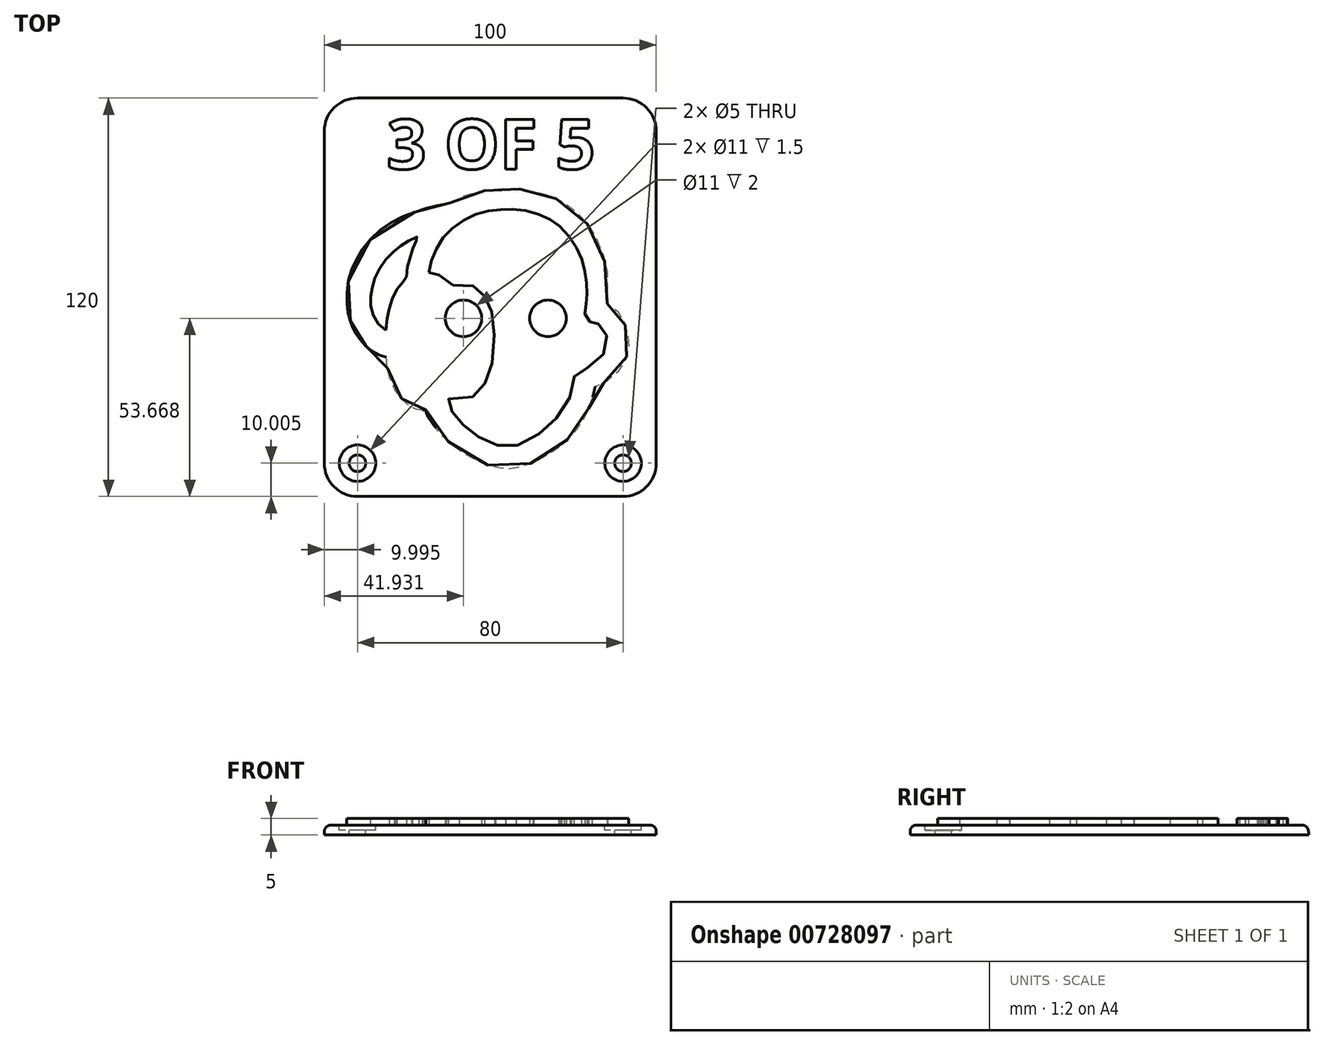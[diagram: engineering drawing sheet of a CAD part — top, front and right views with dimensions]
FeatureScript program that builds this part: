
annotation { "Feature Type Name" : "Feature", "Feature Type Description" : "" }
export const myFeature = defineFeature(function(context is Context, id is Id, definition is map)
    precondition{}
    {
        {
            var Q0;
            Q0=qCreatedBy(makeId("Top.planeOp"),FACE);
            var sketch = newSketch(context, id + "F0", { "sketchPlane" : qUnion([Q0])});
            skLineSegment(sketch, "E0.bottom", {"start": v(-46.51, 69.3) * mm, "end": v(33.49, 69.3) * mm});
            skLineSegment(sketch, "E0.top", {"start": v(-46.51, -50.7) * mm, "end": v(33.49, -50.7) * mm});
            skLineSegment(sketch, "E0.left", {"start": v(-56.51, 59.3) * mm, "end": v(-56.51, -40.7) * mm});
            skLineSegment(sketch, "E0.right", {"start": v(43.49, 59.3) * mm, "end": v(43.49, -40.7) * mm});
            skPoint(sketch, "E1.visualSharp", {"position": v(-56.51, 69.3) * mm});
            skArc(sketch, "E1.filletArc", {"start": v(-46.51, 69.3) * mm, "mid": v(-53.59, 66.38) * mm, "end": v(-56.51, 59.3) * mm});
            skPoint(sketch, "E2.visualSharp", {"position": v(43.49, 69.3) * mm});
            skArc(sketch, "E2.filletArc", {"start": v(43.49, 59.3) * mm, "mid": v(40.56, 66.38) * mm, "end": v(33.49, 69.3) * mm});
            skPoint(sketch, "E3.visualSharp", {"position": v(-56.51, -50.7) * mm});
            skArc(sketch, "E3.filletArc", {"start": v(-56.51, -40.7) * mm, "mid": v(-53.59, -47.77) * mm, "end": v(-46.51, -50.7) * mm});
            skPoint(sketch, "E4.visualSharp", {"position": v(43.49, -50.7) * mm});
            skArc(sketch, "E4.filletArc", {"start": v(33.49, -50.7) * mm, "mid": v(40.56, -47.77) * mm, "end": v(43.49, -40.7) * mm});
            skSolve(sketch);
        }
        {
            var Q0;
            Q0 = qSketchRegion(id + "F0", true);
            extrude(context, id + "F1", {"entities" : qUnion([Q0]), "depth" : 3 * mm, "offsetDistance" : 25 * mm});
        }
        {
            var Q0;
            Q0=makeQuery(id+"F1.opExtrude","CAP_FACE",FACE,{"disambiguationData":[OSD([sQuery(id+"F0.wireOp",EDGE,"E0.bottom"),sQuery(id+"F0.wireOp",EDGE,"E0.top"),sQuery(id+"F0.wireOp",EDGE,"E0.left"),sQuery(id+"F0.wireOp",EDGE,"E0.right")])],"isStart":false});
            var sketch = newSketch(context, id + "F2", { "sketchPlane" : qUnion([Q0])});
            skFitSpline(sketch, "E5", {"points": [v(-25.07, 16.79) * mm, v(-23.95, 21.02) * mm, v(-21.7, 25.75) * mm, v(-18.34, 29.73) * mm, v(-13.49, 33.1) * mm, v(-8.76, 34.96) * mm, v(-3.78, 35.7) * mm, v(0, 35.83) * mm, v(5.54, 35.09) * mm, v(10.56, 33.2) * mm, v(14.02, 30.98) * mm, v(17.76, 26.87) * mm, v(20.5, 22.26) * mm, v(21.92, 17.56) * mm, v(22.5, 13.37) * mm, v(22.6, 9.8) * mm, v(22.28, 6.72) * mm, v(22.08, 3.84) * mm, v(23.6, 1.85) * mm, v(26.1, 1.25) * mm], "startDerivative": vector(17.63, 78.8) * mm, "endDerivative": vector(72.1, -32.78) * mm});
            skFitSpline(sketch, "E6", {"points": [v(26.1, 1.25) * mm, v(26.68, 0.97) * mm, v(27.3, 0.48) * mm, v(27.8, -0.36) * mm, v(28.13, -1.04) * mm, v(28.4, -1.76) * mm, v(28.71, -2.9) * mm, v(28.77, -4.2) * mm, v(28.58, -5.64) * mm, v(28.2, -6.83) * mm, v(27.44, -8) * mm, v(26.4, -9.15) * mm, v(24.92, -10.44) * mm, v(23.87, -11.27) * mm, v(22.55, -12) * mm, v(21.27, -12.13) * mm, v(20.46, -12.4) * mm, v(19.66, -12.89) * mm, v(19.16, -13.65) * mm, v(18.78, -14.9) * mm, v(18.63, -16.3) * mm, v(18.59, -17.55) * mm, v(18, -19.6) * mm, v(17.12, -21.66) * mm, v(16.06, -23.69) * mm, v(14.7, -25.67) * mm, v(13.38, -27.2) * mm, v(12.1, -28.57) * mm, v(10.52, -30.02) * mm, v(9.07, -31.12) * mm, v(7.35, -32.36) * mm, v(5.5, -33.41) * mm, v(2.92, -34.68) * mm, v(1.71, -35.23) * mm, v(0.27, -35.65) * mm, v(-0.64, -35.78) * mm, v(-2.05, -35.8) * mm, v(-3.83, -35.5) * mm, v(-5.21, -35.07) * mm, v(-6.81, -34.41) * mm, v(-8.49, -33.55) * mm, v(-9.64, -32.95) * mm, v(-10.87, -32.21) * mm, v(-12, -31.43) * mm, v(-12.96, -30.64) * mm, v(-13.98, -29.7) * mm, v(-14.79, -28.98) * mm, v(-15.62, -28.12) * mm, v(-16.35, -27.27) * mm, v(-17.16, -26.3) * mm, v(-17.82, -25.44) * mm, v(-18.46, -24.6) * mm, v(-18.99, -23.77) * mm, v(-19.5, -22.87) * mm, v(-19.8, -22.23) * mm, v(-19.76, -21.68) * mm, v(-18.92, -21.3) * mm, v(-18.3, -21.07) * mm, v(-17.58, -20.66) * mm, v(-16.72, -20.66) * mm, v(-11.7, -20.62) * mm, v(-10.67, -20.14) * mm, v(-10.07, -19.5) * mm, v(-9.23, -18.44) * mm, v(-8.55, -17.35) * mm, v(-7.7, -15.82) * mm, v(-7.05, -14.33) * mm, v(-6.59, -12.83) * mm, v(-6.15, -11.25) * mm, v(-5.76, -8.98) * mm, v(-5.51, -5.8) * mm, v(-5.33, -3) * mm, v(-5.26, 0) * mm, v(-5.35, 1.51) * mm, v(-5.66, 3.34) * mm, v(-6.08, 5.06) * mm, v(-6.48, 6.3) * mm, v(-7, 7.46) * mm, v(-7.48, 8.45) * mm, v(-7.84, 9.08) * mm, v(-8.32, 9.84) * mm, v(-8.76, 10.44) * mm, v(-9.2, 11) * mm, v(-9.86, 11.62) * mm, v(-10.78, 12.25) * mm, v(-11.49, 12.66) * mm, v(-12.24, 12.87) * mm, v(-14.3, 12.85) * mm, v(-15.8, 12.81) * mm, v(-17.19, 12.86) * mm, v(-18.31, 13.27) * mm, v(-19.4, 13.91) * mm, v(-20.33, 14.64) * mm, v(-21.03, 15.21) * mm, v(-21.74, 15.8) * mm, v(-22.29, 16.27) * mm, v(-22.8, 16.68) * mm, v(-23.06, 16.73) * mm, v(-23.62, 16.73) * mm, v(-24.15, 16.72) * mm, v(-24.51, 16.71) * mm, v(-24.87, 16.7) * mm, v(-25.07, 16.79) * mm], "startDerivative": vector(82.47, -38.35) * mm, "endDerivative": vector(-44.86, 24.31) * mm});
            skCircle(sketch, "E7", {"center": v(10.87, 2.97) * mm, "radius": 5.5 * mm});
            skCircle(sketch, "E8", {"center": v(-14.58, 2.97) * mm, "radius": 5.5 * mm});
            skFitSpline(sketch, "E9", {"points": [v(-38, -0.58) * mm, v(-37.64, 1.98) * mm, v(-37.38, 3.87) * mm, v(-37, 5.76) * mm, v(-36.45, 7.58) * mm, v(-35.75, 9.54) * mm, v(-34.82, 11.35) * mm, v(-33.53, 13.16) * mm, v(-32.54, 14.12) * mm, v(-31.76, 14.77) * mm, v(-31.76, 15.08) * mm, v(-31.72, 16.59) * mm, v(-31.45, 18.32) * mm, v(-30.95, 20.4) * mm, v(-30.49, 22.08) * mm, v(-30.08, 23.36) * mm, v(-29.52, 24.73) * mm, v(-28.96, 25.97) * mm, v(-28.5, 26.8) * mm, v(-28.1, 27.5) * mm, v(-28.62, 27.5) * mm, v(-29.9, 27.02) * mm, v(-31.27, 26.18) * mm, v(-32.84, 25.24) * mm, v(-34.1, 24.28) * mm, v(-35.4, 23.24) * mm, v(-36.69, 22.06) * mm, v(-38.17, 20.35) * mm, v(-39.61, 18.35) * mm, v(-40.61, 16.47) * mm, v(-41.35, 14.84) * mm, v(-41.87, 13.17) * mm, v(-42.24, 11.58) * mm, v(-42.53, 10.14) * mm, v(-42.65, 8.25) * mm, v(-42.53, 6.73) * mm, v(-42.2, 5.22) * mm, v(-41.6, 3.55) * mm, v(-40.52, 1.67) * mm, v(-39.42, 0.36) * mm, v(-38, -0.58) * mm]});
            skFitSpline(sketch, "E10", {"points": [v(-18.62, 37.66) * mm, v(-16.92, 38.6) * mm, v(-14.64, 39.75) * mm, v(-13.25, 40.33) * mm, v(-11.24, 40.9) * mm, v(-9.63, 41.2) * mm, v(-8.04, 41.5) * mm, v(-6.02, 41.8) * mm, v(-4.3, 41.97) * mm, v(-2.64, 42.04) * mm, v(-0.91, 42.1) * mm, v(1, 42.08) * mm, v(2.14, 41.93) * mm, v(4, 41.67) * mm, v(5.87, 41.33) * mm, v(8.27, 40.8) * mm, v(10.16, 40.3) * mm, v(11.97, 39.62) * mm, v(14.02, 38.75) * mm, v(16.14, 37.6) * mm, v(17.5, 36.5) * mm, v(19.07, 35.26) * mm, v(21.02, 33.41) * mm, v(22.76, 31.4) * mm, v(24.07, 29.42) * mm, v(25.4, 27.09) * mm, v(26.26, 25.01) * mm, v(27.24, 22.7) * mm, v(27.86, 20.46) * mm, v(28.4, 18.36) * mm, v(28.77, 16.06) * mm, v(28.77, 13.55) * mm, v(28.77, 10.18) * mm, v(28.77, 7.69) * mm, v(28.77, 7.22) * mm, v(29.81, 6.63) * mm, v(30.76, 6.03) * mm, v(31.77, 5.2) * mm, v(32.48, 4.31) * mm, v(33.07, 3.34) * mm, v(33.67, 2.02) * mm, v(34.22, 0.77) * mm, v(34.68, -0.5) * mm, v(34.88, -2.12) * mm, v(35.08, -3.59) * mm, v(35.18, -4.97) * mm, v(35.13, -6.42) * mm, v(34.8, -7.8) * mm, v(34.35, -9.14) * mm, v(33.64, -10.74) * mm, v(32.45, -12.46) * mm, v(31.18, -13.87) * mm, v(29.81, -15.1) * mm, v(28.4, -16.16) * mm, v(26.86, -17.04) * mm, v(25.67, -17.6) * mm, v(25.13, -17.74) * mm, v(24.92, -18.34) * mm, v(24.42, -20.49) * mm, v(23.92, -22.01) * mm, v(23.42, -23.32) * mm, v(23.02, -24.36) * mm, v(22.22, -26.08) * mm, v(21.26, -27.82) * mm, v(20.2, -29.41) * mm, v(18.95, -31.1) * mm, v(17.4, -32.8) * mm, v(15.69, -34.55) * mm, v(13.57, -36.35) * mm, v(11.11, -38) * mm, v(8.59, -39.4) * mm, v(6.38, -40.43) * mm, v(3.95, -41.36) * mm, v(1.59, -42.02) * mm, v(-0.31, -42.36) * mm, v(-2.99, -42.3) * mm, v(-6.35, -41.58) * mm, v(-9.09, -40.52) * mm, v(-11.49, -39.4) * mm, v(-13.97, -38.03) * mm, v(-16.49, -36.34) * mm, v(-19.23, -34.05) * mm, v(-21.15, -32.27) * mm, v(-22.93, -30.02) * mm, v(-24.85, -27.39) * mm, v(-25.72, -25.67) * mm, v(-25.88, -24.95) * mm, v(-25.9, -24.64) * mm, v(-26.27, -24.63) * mm, v(-27.36, -24.61) * mm, v(-28.52, -24.5) * mm, v(-29.86, -23.98) * mm, v(-31.02, -23.28) * mm, v(-31.86, -22.62) * mm, v(-32.6, -22) * mm, v(-33.27, -21.23) * mm, v(-34.12, -20.24) * mm, v(-34.93, -18.93) * mm, v(-35.73, -17.4) * mm, v(-36.33, -15.88) * mm, v(-36.92, -14.36) * mm, v(-37.32, -12.52) * mm, v(-37.66, -10.81) * mm, v(-37.88, -8.76) * mm, v(-38.17, -8.76) * mm, v(-39.56, -8.26) * mm, v(-41.55, -7.3) * mm, v(-42.99, -6.27) * mm, v(-43.96, -5.41) * mm, v(-44.81, -4.45) * mm, v(-45.67, -3.49) * mm, v(-46.42, -2.52) * mm, v(-47.1, -1.54) * mm, v(-47.68, -0.45) * mm, v(-48.2, 0.79) * mm, v(-48.63, 2) * mm, v(-49.01, 3.34) * mm, v(-49.31, 4.66) * mm, v(-49.53, 6.11) * mm, v(-49.73, 7.98) * mm, v(-49.65, 11.28) * mm, v(-49.19, 14.76) * mm, v(-48.35, 17.44) * mm, v(-47.29, 19.9) * mm, v(-45.76, 22.6) * mm, v(-43.59, 25.63) * mm, v(-40.65, 28.64) * mm, v(-37.71, 30.98) * mm, v(-34.37, 32.93) * mm, v(-30.44, 34.55) * mm, v(-27.8, 35.47) * mm, v(-24.69, 36.42) * mm, v(-22.48, 36.9) * mm, v(-20.63, 37.26) * mm, v(-19.35, 37.42) * mm, v(-18.76, 37.47) * mm, v(-18.62, 37.66) * mm]});
            skSolve(sketch);
        }
        {
            var Q0;
            Q0 = qSketchRegion(id + "F2", true);
            var Q1;
            Q1=makeQuery(id+"F2.imprint","IMPRINT",FACE,{"disambiguationData":[TD([[makeQuery(id+"F2.imprint","IMPRINT",EDGE,{"derivedFrom":sQuery(id+"F2.wireOp",EDGE,"E7")}),1.0]])]});
            extrude(context, id + "F3", {"entities" : qUnion([Q0, Q1]), "operationType" : NewBodyOperationType.ADD, "depth" : 2 * mm, "offsetDistance" : 25 * mm});
        }
        {
            var Q0;
            {var subQ0=sQuery(id+"F0.wireOp",EDGE,"E0.left");var subQ1=sQuery(id+"F0.wireOp",EDGE,"E0.top");var subQ2=sQuery(id+"F0.wireOp",EDGE,"E0.right");var subQ3=sQuery(id+"F0.wireOp",EDGE,"E0.bottom");var subQ4=sQuery(id+"F0.wireOp",EDGE,"E1.filletArc");var subQ5=sQuery(id+"F0.wireOp",EDGE,"E2.filletArc");var subQ6=sQuery(id+"F0.wireOp",EDGE,"E3.filletArc");var subQ7=sQuery(id+"F0.wireOp",EDGE,"E4.filletArc");Q0=makeQuery(id+"F3.boolean.opBoolean","SPLIT",FACE,{"disambiguationData":[TD([makeQuery(id+"F1.opExtrude","SWEPT_FACE",FACE,{"disambiguationData":[OSD([subQ3])]})])],"derivedFrom":makeQuery(id+"F1.opExtrude","CAP_FACE",FACE,{"disambiguationData":[OSD([subQ3,subQ1,subQ0,subQ2,subQ4,subQ5,subQ6,subQ7])],"isStart":false})});}
            var sketch = newSketch(context, id + "F4", { "sketchPlane" : qUnion([Q0])});
            skLineSegment(sketch, "E11", {"start": v(-78.45, -40.7) * mm, "end": v(78.05, -40.7) * mm, "construction": true});
            skCircle(sketch, "E12", {"center": v(-46.51, -40.7) * mm, "radius": 2.5 * mm});
            skCircle(sketch, "E13", {"center": v(33.49, -40.7) * mm, "radius": 2.5 * mm});
            skCircle(sketch, "E14.0", {"center": v(-46.51, -40.7) * mm, "radius": 5.5 * mm});
            skCircle(sketch, "E15.0", {"center": v(33.49, -40.7) * mm, "radius": 5.5 * mm});
            skSolve(sketch);
        }
        {
            var Q0;
            Q0=makeQuery(id+"F4.imprint","IMPRINT",FACE,{"disambiguationData":[TD([[makeQuery(id+"F4.imprint","IMPRINT",EDGE,{"derivedFrom":sQuery(id+"F4.wireOp",EDGE,"E12")}),1.0]])]});
            var Q1;
            Q1=makeQuery(id+"F4.imprint","IMPRINT",FACE,{"disambiguationData":[TD([[makeQuery(id+"F4.imprint","IMPRINT",EDGE,{"derivedFrom":sQuery(id+"F4.wireOp",EDGE,"E13")}),1.0]])]});
            extrude(context, id + "F5", {"entities" : qUnion([Q0, Q1]), "operationType" : NewBodyOperationType.REMOVE, "oppositeDirection" : true, "depth" : 25 * mm, "offsetDistance" : 25 * mm});
        }
        {
            var Q0;
            Q0=makeQuery(id+"F4.imprint","IMPRINT",FACE,{"disambiguationData":[TD([[makeQuery(id+"F4.imprint","IMPRINT",EDGE,{"derivedFrom":sQuery(id+"F4.wireOp",EDGE,"E12")}),-1.0]])]});
            var Q1;
            Q1=makeQuery(id+"F4.imprint","IMPRINT",FACE,{"disambiguationData":[TD([[makeQuery(id+"F4.imprint","IMPRINT",EDGE,{"derivedFrom":sQuery(id+"F4.wireOp",EDGE,"E13")}),-1.0]])]});
            extrude(context, id + "F6", {"entities" : qUnion([Q0, Q1]), "operationType" : NewBodyOperationType.REMOVE, "oppositeDirection" : true, "depth" : 1.5 * mm, "offsetDistance" : 25 * mm});
        }
        {
            var Q0;
            Q0=makeQuery(id+"F1.opExtrude","CAP_EDGE",EDGE,{"disambiguationData":[OSD([sQuery(id+"F0.wireOp",EDGE,"E0.top")])],"isStart":false});
            fillet(context, id + "F7", {"entities" : qUnion([Q0]), "radius" : 2 * mm, "tangentPropagation" : true, "allowEdgeOverflow" : false});
        }
        {
            var Q0;
            {var subQ0=sQuery(id+"F0.wireOp",EDGE,"E0.left");var subQ1=sQuery(id+"F0.wireOp",EDGE,"E0.top");var subQ2=sQuery(id+"F0.wireOp",EDGE,"E0.right");var subQ3=sQuery(id+"F0.wireOp",EDGE,"E0.bottom");var subQ4=sQuery(id+"F0.wireOp",EDGE,"E1.filletArc");var subQ5=sQuery(id+"F0.wireOp",EDGE,"E2.filletArc");var subQ6=sQuery(id+"F0.wireOp",EDGE,"E3.filletArc");var subQ7=sQuery(id+"F0.wireOp",EDGE,"E4.filletArc");Q0=makeQuery(id+"F3.boolean.opBoolean","SPLIT",FACE,{"disambiguationData":[TD([makeQuery(id+"F1.opExtrude","SWEPT_FACE",FACE,{"disambiguationData":[OSD([subQ3])]})])],"derivedFrom":makeQuery(id+"F1.opExtrude","CAP_FACE",FACE,{"disambiguationData":[OSD([subQ3,subQ1,subQ0,subQ2,subQ4,subQ5,subQ6,subQ7])],"isStart":false})});}
            var sketch = newSketch(context, id + "F8", { "sketchPlane" : qUnion([Q0])});
            skText(sketch, "E16", { "text": "3 OF 5\n", "fontName": "OpenSans-Bold.ttf"});
            const initialGuessF8  = {"E16": [-0.03773, 0.04792, 1, 0, 0.01504]};
            skSetInitialGuess(sketch, initialGuessF8);
            skSolve(sketch);
        }
        {
            var Q0;
            Q0 = qSketchRegion(id + "F8", true);
            extrude(context, id + "F9", {"entities" : qUnion([Q0]), "operationType" : NewBodyOperationType.ADD, "depth" : 2 * mm, "offsetDistance" : 25 * mm});
        }
    });
